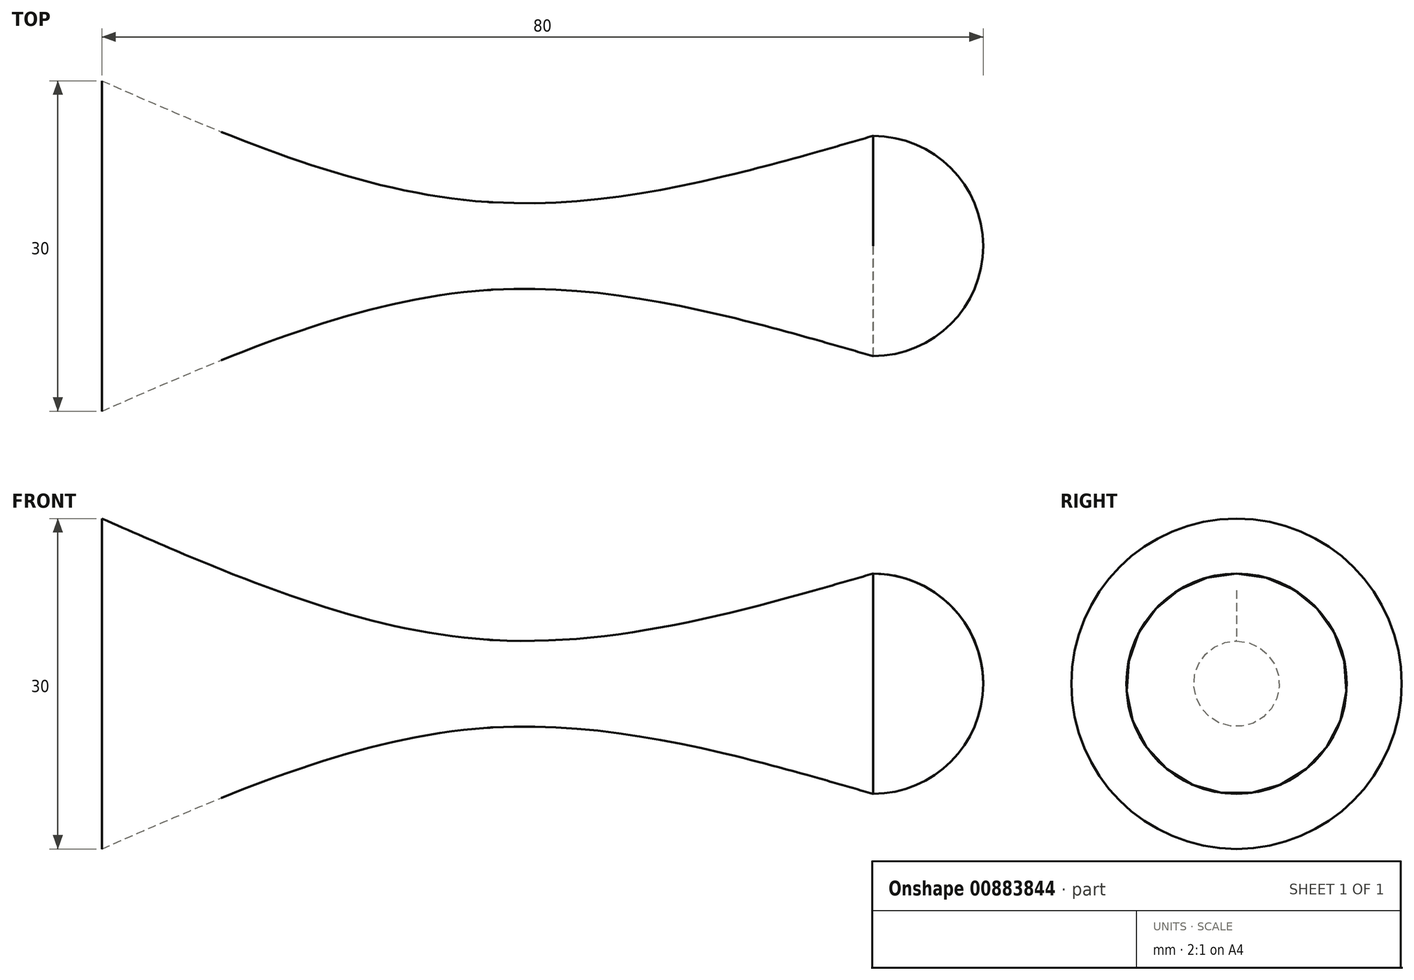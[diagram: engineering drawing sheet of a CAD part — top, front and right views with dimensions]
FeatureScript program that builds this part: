
annotation { "Feature Type Name" : "Feature", "Feature Type Description" : "" }
export const myFeature = defineFeature(function(context is Context, id is Id, definition is map)
    precondition{}
    {
        {
            var Q0;
            Q0=qCreatedBy(makeId("Top.planeOp"),FACE);
            var sketch = newSketch(context, id + "F0", { "sketchPlane" : qUnion([Q0])});
            skLineSegment(sketch, "E0.bottom", {"start": v(-65, 35) * mm, "end": v(65, 35) * mm});
            skLineSegment(sketch, "E0.top", {"start": v(-65, -35) * mm, "end": v(65, -35) * mm});
            skLineSegment(sketch, "E0.left", {"start": v(-65, 35) * mm, "end": v(-65, -35) * mm});
            skLineSegment(sketch, "E0.right", {"start": v(65, 35) * mm, "end": v(65, -35) * mm});
            skPoint(sketch, "E0.middle", {"position": v(0, 0) * mm});
            skLineSegment(sketch, "E1", {"start": v(-62, -35) * mm, "end": v(-62, 35) * mm});
            skLineSegment(sketch, "E2", {"start": v(-65, 32) * mm, "end": v(65, 32) * mm});
            skLineSegment(sketch, "E3.MirrorCS", {"start": v(-65, -32) * mm, "end": v(65, -32) * mm});
            skLineSegment(sketch, "E4.MirrorCS", {"start": v(62, -35) * mm, "end": v(62, 35) * mm});
            skSolve(sketch);
        }
        {
            var Q0;
            Q0=qCreatedBy(makeId("Top.planeOp"),FACE);
            var sketch = newSketch(context, id + "F1", { "sketchPlane" : qUnion([Q0])});
            skLineSegment(sketch, "E5.0", {"start": v(-65, 35) * mm, "end": v(65, 35) * mm});
            skLineSegment(sketch, "E5.1", {"start": v(-65, 35) * mm, "end": v(-65, -35) * mm});
            skLineSegment(sketch, "E5.2", {"start": v(-65, -35) * mm, "end": v(65, -35) * mm});
            skLineSegment(sketch, "E5.3", {"start": v(65, 35) * mm, "end": v(65, -35) * mm});
            skLineSegment(sketch, "E6", {"start": v(0, 35) * mm, "end": v(0, -35) * mm});
            skLineSegment(sketch, "E7", {"start": v(-3, -35) * mm, "end": v(-3, 35) * mm});
            skLineSegment(sketch, "E8", {"start": v(0, 0) * mm, "end": v(-65, 0) * mm, "construction": true});
            skSolve(sketch);
        }
        {
            var Q0;
            Q0=sQuery(id+"F1.wireOp",EDGE,"E8");
            cPlane(context, id + "F2", {"entities" : qUnion([Q0]), "cplaneType" : CPlaneType.LINE_ANGLE, "offset" : 25 * mm, "angle" : 0 * degree, "width" : 150 * mm, "height" : 150 * mm});
        }
        {
            var Q0;
            Q0=qCreatedBy(id+"F2.planeOp",FACE);
            var sketch = newSketch(context, id + "F3", { "sketchPlane" : qUnion([Q0])});
            skLineSegment(sketch, "E9", {"start": v(0, 1.33) * mm, "end": v(0, 21.33) * mm, "construction": true});
            skLineSegment(sketch, "E10", {"start": v(0, 21.33) * mm, "end": v(35, 21.33) * mm, "construction": true});
            skLineSegment(sketch, "E11", {"start": v(0, 21.33) * mm, "end": v(-35, 21.33) * mm, "construction": true});
            skCircle(sketch, "E12", {"center": v(35, 21.33) * mm, "radius": 10 * mm});
            skCircle(sketch, "E13", {"center": v(0, 21.33) * mm, "radius": 4 * mm});
            skCircle(sketch, "E14", {"center": v(-35, 21.33) * mm, "radius": 15 * mm});
            skFitSpline(sketch, "E15", {"points": [v(35, 31.33) * mm, v(0, 25.33) * mm, v(-35, 36.33) * mm], "startDerivative": vector(-70.86, -20.5) * mm, "endDerivative": vector(-69.15, 30.37) * mm});
            skLineSegment(sketch, "E16", {"start": v(-50, 21.33) * mm, "end": v(45, 21.33) * mm});
            skLineSegment(sketch, "E17", {"start": v(-35, 21.33) * mm, "end": v(-35, 36.33) * mm});
            skSolve(sketch);
        }
        {
            var Q0;
            {var subQ5=sQuery(id+"F3.wireOp",EDGE,"E17");Q0=makeQuery(id+"F3.imprint","IMPRINT",FACE,{"disambiguationData":[TD([[makeQuery(id+"F3.imprint","IMPRINT",EDGE,{"derivedFrom":subQ5}),-1.0]])]});}
            var Q1;
            {var subQ0=sQuery(id+"F3.wireOp",EDGE,"E15");var subQ1=sQuery(id+"F3.wireOp",EDGE,"E13");var subQ2=makeQuery(id+"F3.imprint","INTERSECT",VERTEX,{"disambiguationData":[OD(1.0)],"derivedFrom":[subQ1,subQ0]});Q1=makeQuery(id+"F3.imprint","IMPRINT",FACE,{"disambiguationData":[TD([[makeQuery(id+"F3.imprint","IMPRINT",EDGE,{"disambiguationData":[TD([[subQ2,-1.0]])],"derivedFrom":subQ1}),-1.0]])]});}
            var Q2;
            {var subQ0=sQuery(id+"F3.wireOp",EDGE,"E15");var subQ1=sQuery(id+"F3.wireOp",EDGE,"E13");var subQ2=makeQuery(id+"F3.imprint","INTERSECT",VERTEX,{"disambiguationData":[OD(0.0)],"derivedFrom":[subQ1,subQ0]});Q2=makeQuery(id+"F3.imprint","IMPRINT",FACE,{"disambiguationData":[TD([[makeQuery(id+"F3.imprint","IMPRINT",EDGE,{"disambiguationData":[TD([[subQ2,1.0]])],"derivedFrom":subQ1}),1.0]])]});}
            var Q3;
            {var subQ0=sQuery(id+"F3.wireOp",EDGE,"E15");var subQ1=sQuery(id+"F3.wireOp",EDGE,"E12");var subQ2=makeQuery(id+"F3.imprint","INTERSECT",VERTEX,{"disambiguationData":[OD(1.0)],"derivedFrom":[subQ1,subQ0]});Q3=makeQuery(id+"F3.imprint","IMPRINT",FACE,{"disambiguationData":[TD([[makeQuery(id+"F3.imprint","IMPRINT",EDGE,{"disambiguationData":[TD([[subQ2,-1.0]])],"derivedFrom":subQ1}),-1.0]])]});}
            var Q4;
            {var subQ0=sQuery(id+"F3.wireOp",EDGE,"E15");var subQ1=sQuery(id+"F3.wireOp",EDGE,"E12");var subQ2=makeQuery(id+"F3.imprint","INTERSECT",VERTEX,{"disambiguationData":[OD(0.0)],"derivedFrom":[subQ1,subQ0]});Q4=makeQuery(id+"F3.imprint","IMPRINT",FACE,{"disambiguationData":[TD([[makeQuery(id+"F3.imprint","IMPRINT",EDGE,{"disambiguationData":[TD([[subQ2,1.0]])],"derivedFrom":subQ1}),1.0]])]});}
            var Q5;
            Q5=sQuery(id+"F3.wireOp",EDGE,"E16");
            revolve(context, id + "F4", {"surfaceOperationType" : NewSurfaceOperationType.NEW, "entities" : qUnion([Q0, Q1, Q2, Q3, Q4]), "axis" : qUnion([Q5]), "revolveType" : RevolveType.FULL});
        }
    });
